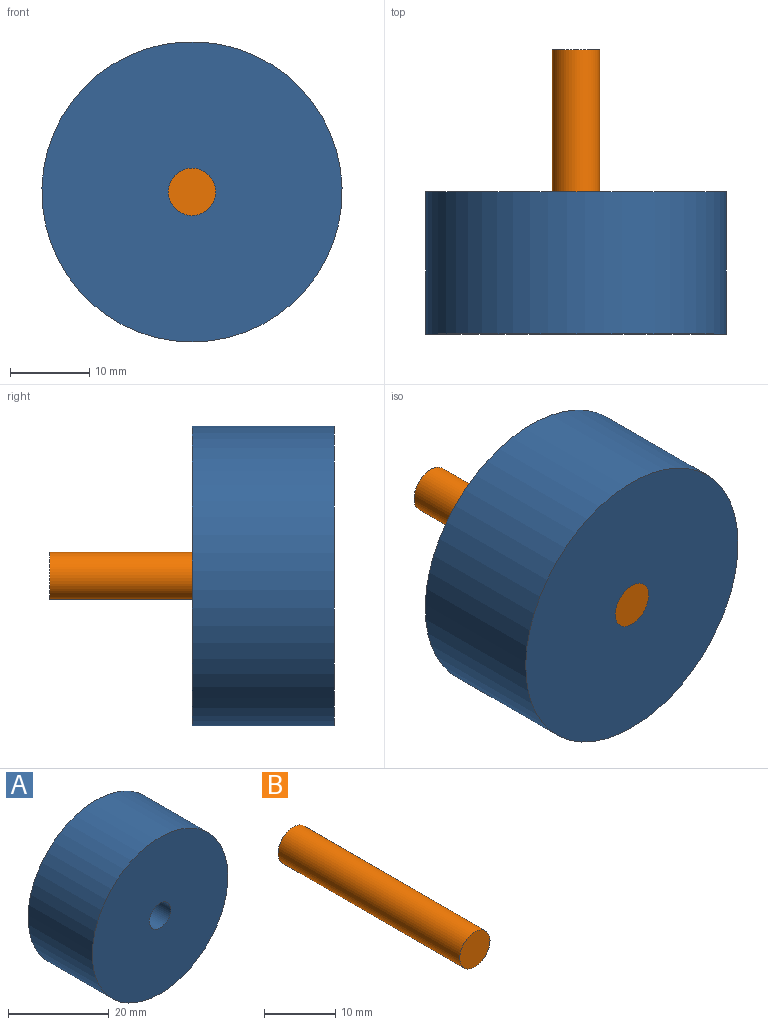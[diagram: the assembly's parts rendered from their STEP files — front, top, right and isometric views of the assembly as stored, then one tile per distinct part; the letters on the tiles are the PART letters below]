
ASSEMBLY  parts=2 mates=1
PART A: 4 faces, bbox 38x18x38 mm
  f0: cylinder r=3mm len=18mm, axis (0,-1,0), area 339.3mm2, adj f2,f3
  f1: cylinder r=19mm len=38mm, axis (0,-1,0), area 2148.8mm2, adj f2,f3
  f2: plane 38x38mm, normal (0,1,0), area 1105.8mm2, adj f0,f1
  f3: plane 38x38mm, normal (0,-1,0), area 1105.8mm2, adj f0,f1
PART B: 3 faces, bbox 6x36x6 mm
  f0: cylinder r=3mm len=36mm, axis (0,1,0), area 678.6mm2, adj f1,f2
  f1: plane 6x6mm, normal (0,-1,0), area 28.3mm2, adj f0
  f2: plane 6x6mm, normal (0,1,0), area 28.3mm2, adj f0
PLACE A at identity fixed
PLACE B t=(0,36,0)mm
MATE revolute A.f0 <-> B.f0  axis (0,-1,0) through (0,0,0)mm
